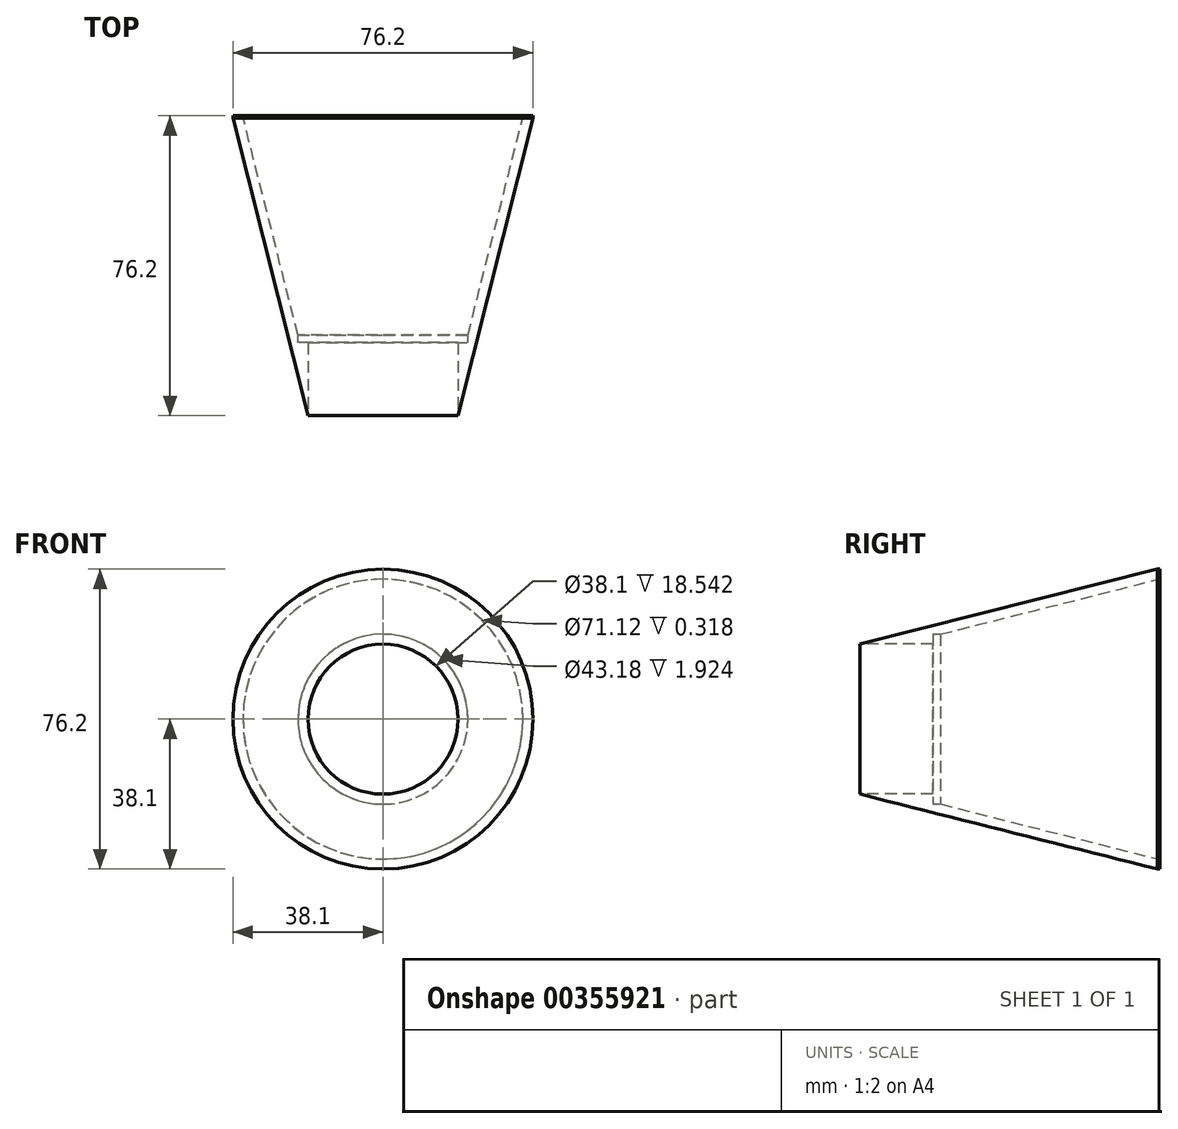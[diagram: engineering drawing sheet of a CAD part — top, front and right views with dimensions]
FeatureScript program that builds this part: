
annotation { "Feature Type Name" : "Feature", "Feature Type Description" : "" }
export const myFeature = defineFeature(function(context is Context, id is Id, definition is map)
    precondition{}
    {
        {
            var Q0;
            Q0=qCreatedBy(makeId("Front.planeOp"),FACE);
            var sketch = newSketch(context, id + "F0", { "sketchPlane" : qUnion([Q0])});
            skCircle(sketch, "E0", {"center": v(0, 0) * mm, "radius": 19.05 * mm});
            skCircle(sketch, "E1", {"center": v(0, 0) * mm, "radius": 38.1 * mm});
            skSolve(sketch);
        }
        {
            var Q0;
            Q0=qSketchRegion(id+"F0",true);
            extrude(context, id + "F1", {"entities" : qUnion([Q0]), "oppositeDirection" : true, "depth" : 76.2 * mm});
        }
        {
            var Q0;
            Q0=qCreatedBy(makeId("Right.planeOp"),FACE);
            var sketch = newSketch(context, id + "F2", { "sketchPlane" : qUnion([Q0])});
            skLineSegment(sketch, "E2", {"start": v(0, 0) * mm, "end": v(0, 19.05) * mm});
            skLineSegment(sketch, "E3", {"start": v(0, 19.05) * mm, "end": v(89.66, 41.65) * mm});
            skLineSegment(sketch, "E4", {"start": v(89.66, 41.65) * mm, "end": v(-15.24, 41.65) * mm});
            skLineSegment(sketch, "E5", {"start": v(-15.24, 41.65) * mm, "end": v(0, 19.05) * mm});
            skSolve(sketch);
        }
        {
            var Q0;
            Q0=qSketchRegion(id+"F2",true);
            var Q1;
            Q1=makeQuery(id+"F1.opExtrude","CAP_EDGE",EDGE,{"disambiguationData":[OSD([sQuery(id+"F0.wireOp",EDGE,"E1")])],"isStart":false});
            revolve(context, id + "F3", {"operationType" : NewBodyOperationType.REMOVE, "entities" : qUnion([Q0]), "axis" : qUnion([Q1]), "revolveType" : RevolveType.FULL, "oppositeDirection" : true});
        }
        {
            var Q0;
            Q0=makeQuery(id+"F1.opExtrude","CAP_FACE",FACE,{"disambiguationData":[OSD([sQuery(id+"F0.wireOp",EDGE,"E0"),sQuery(id+"F0.wireOp",EDGE,"E1")])],"isStart":false});
            shell(context, id + "F4", {"entities" : qUnion([Q0]), "thickness" : 2.54 * mm});
        }
        {
            var Q0;
            Q0=makeQuery(id+"F4.opShell","OFFSET_FACE",FACE,{"disambiguationData":[OSD([sQuery(id+"F0.wireOp",EDGE,"E0"),sQuery(id+"F0.wireOp",EDGE,"E1")])]});
            extrude(context, id + "F5", {"entities" : qUnion([Q0]), "operationType" : NewBodyOperationType.REMOVE, "oppositeDirection" : true, "depth" : 57.66 * mm});
        }
    });
